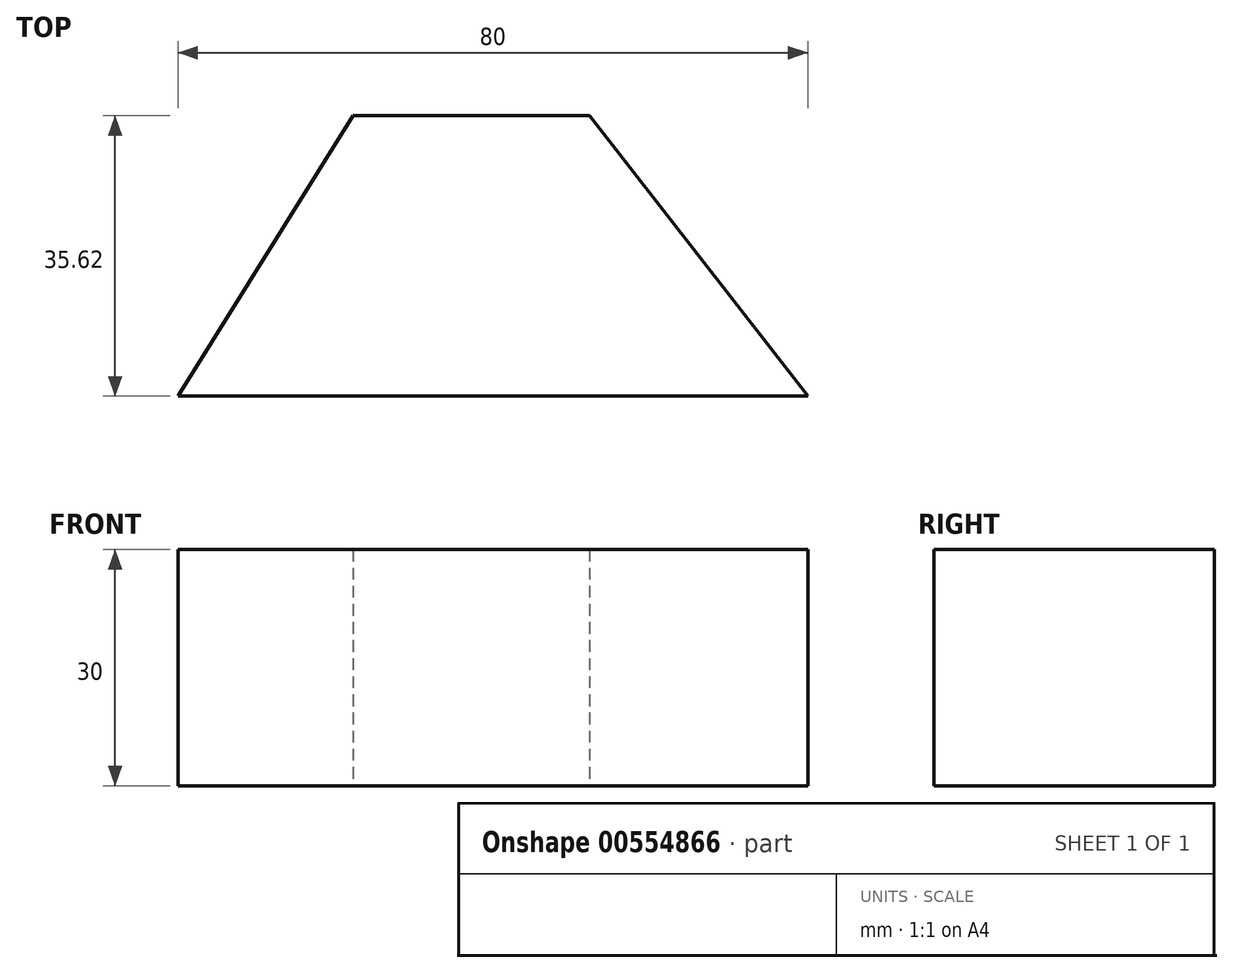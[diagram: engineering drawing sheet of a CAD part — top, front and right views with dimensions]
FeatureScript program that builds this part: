
annotation { "Feature Type Name" : "Feature", "Feature Type Description" : "" }
export const myFeature = defineFeature(function(context is Context, id is Id, definition is map)
    precondition{}
    {
        {
            var Q0;
            Q0=qCreatedBy(makeId("Top.planeOp"),FACE);
            var sketch = newSketch(context, id + "F0", { "sketchPlane" : qUnion([Q0])});
            skLineSegment(sketch, "E0", {"start": v(-18.61, 30.15) * mm, "end": v(11.39, 30.15) * mm});
            skLineSegment(sketch, "E1", {"start": v(-18.61, 30.15) * mm, "end": v(-40.87, -5.47) * mm});
            skLineSegment(sketch, "E2", {"start": v(-40.87, -5.47) * mm, "end": v(39.13, -5.47) * mm});
            skLineSegment(sketch, "E3", {"start": v(11.39, 30.15) * mm, "end": v(39.13, -5.47) * mm});
            skSolve(sketch);
        }
        {
            var Q0;
            Q0=makeQuery(id+"F0.imprint","IMPRINT",FACE,{"disambiguationData":[TD([[makeQuery(id+"F0.imprint","IMPRINT",EDGE,{"derivedFrom":sQuery(id+"F0.wireOp",EDGE,"E0")}),-1.0]])]});
            extrude(context, id + "F1", {"entities" : qUnion([Q0]), "depth" : 30 * mm, "offsetDistance" : 25 * mm});
        }
    });
